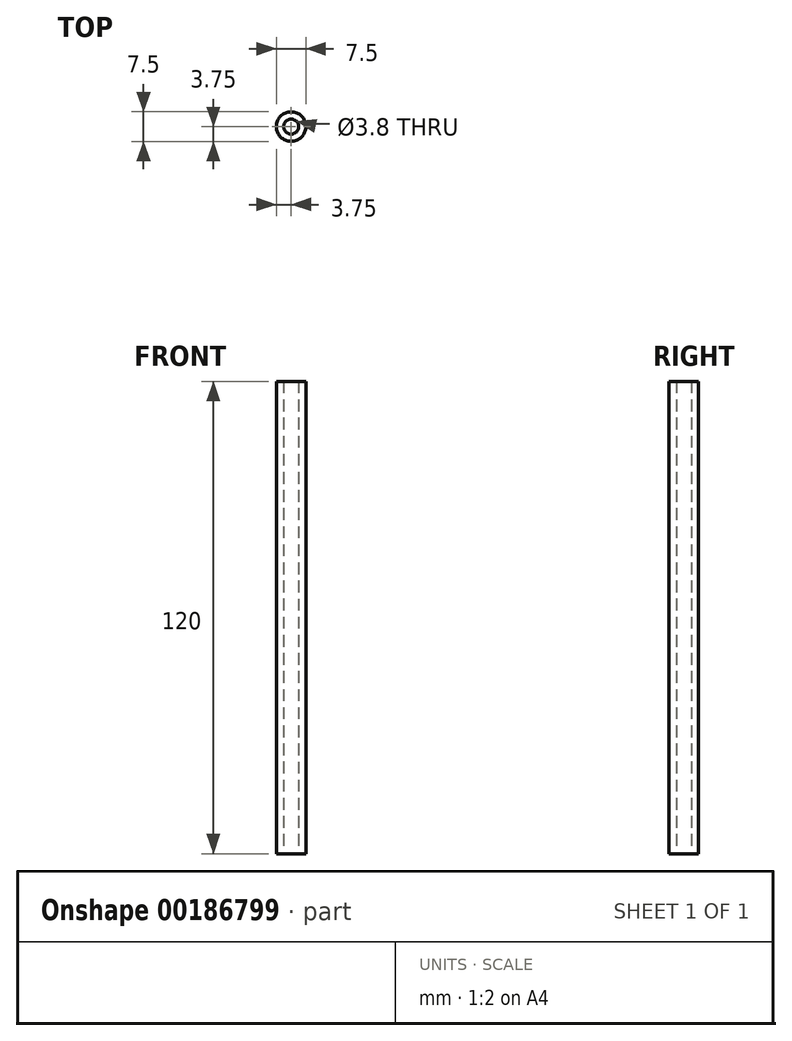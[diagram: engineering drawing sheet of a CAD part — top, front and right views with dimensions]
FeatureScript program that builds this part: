
annotation { "Feature Type Name" : "Feature", "Feature Type Description" : "" }
export const myFeature = defineFeature(function(context is Context, id is Id, definition is map)
    precondition{}
    {
        {
            var Q0;
            Q0=qCreatedBy(makeId("Top.planeOp"),FACE);
            var sketch = newSketch(context, id + "F0", { "sketchPlane" : qUnion([Q0])});
            skCircle(sketch, "E0", {"center": v(0, 0) * mm, "radius": 3.75 * mm});
            skCircle(sketch, "E1", {"center": v(0, 0) * mm, "radius": 1.9 * mm});
            skSolve(sketch);
        }
        {
            var Q0;
            Q0=makeQuery(id+"F0.imprint","IMPRINT",FACE,{"disambiguationData":[TD([[makeQuery(id+"F0.imprint","IMPRINT",EDGE,{"derivedFrom":sQuery(id+"F0.wireOp",EDGE,"E0")}),1.0]])]});
            extrude(context, id + "F1", {"entities" : qUnion([Q0]), "depth" : 120 * mm});
        }
    });
